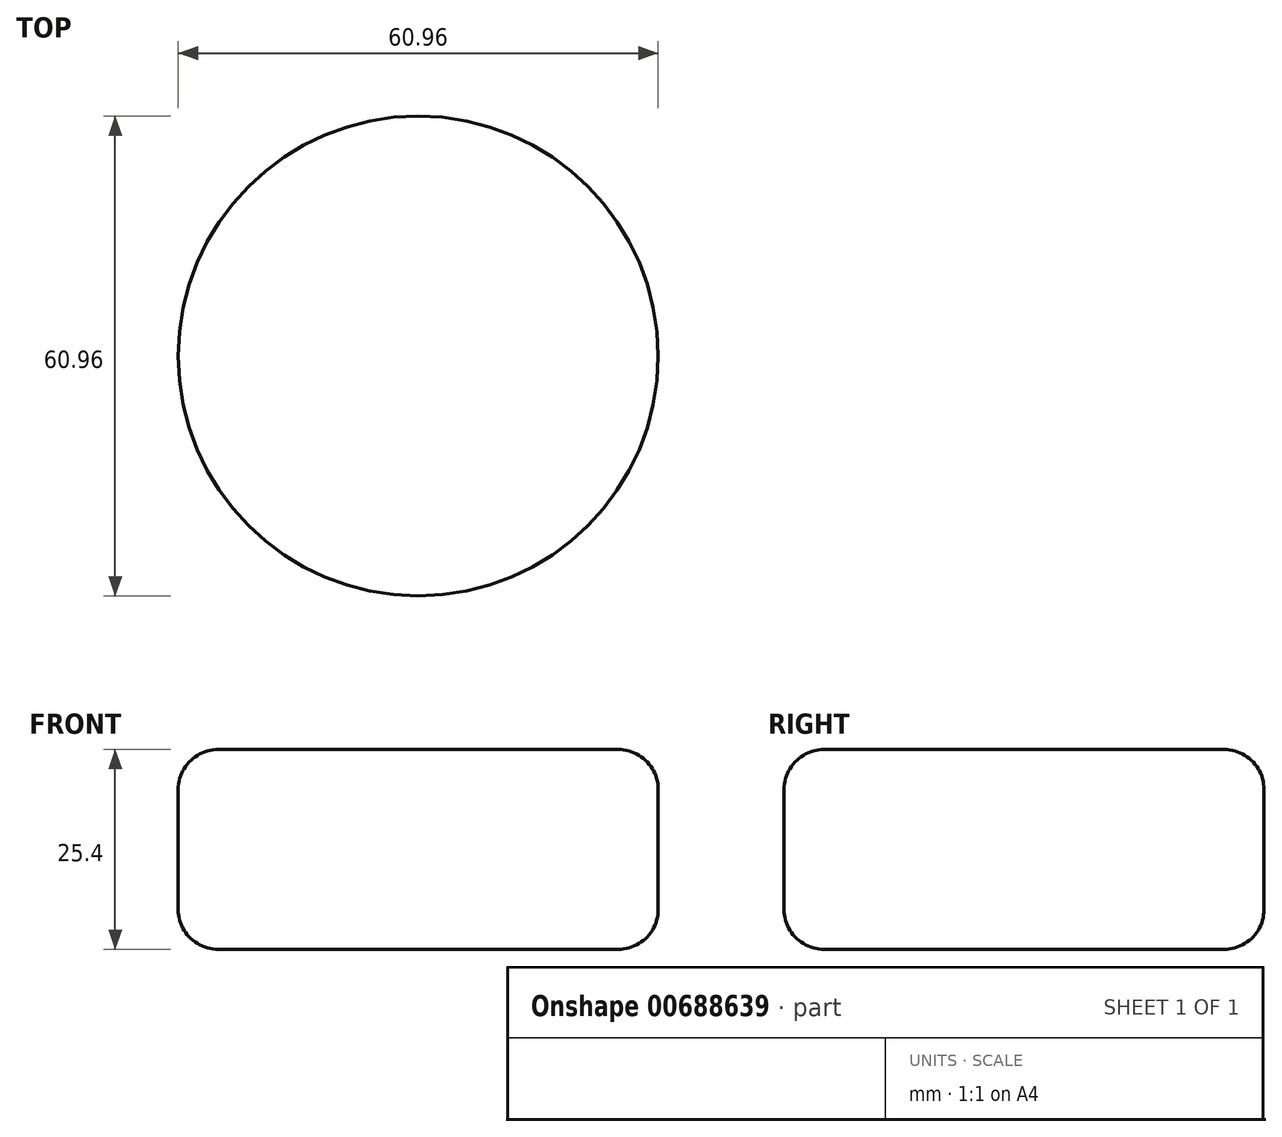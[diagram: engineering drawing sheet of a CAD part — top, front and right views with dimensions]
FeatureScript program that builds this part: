
annotation { "Feature Type Name" : "Feature", "Feature Type Description" : "" }
export const myFeature = defineFeature(function(context is Context, id is Id, definition is map)
    precondition{}
    {
        {
            var Q0;
            Q0=qCreatedBy(makeId("Top.planeOp"),FACE);
            var sketch = newSketch(context, id + "F0", { "sketchPlane" : qUnion([Q0])});
            skCircle(sketch, "E0", {"center": v(0, 0) * mm, "radius": 30.48 * mm});
            skSolve(sketch);
        }
        {
            var Q0;
            Q0 = qSketchRegion(id + "F0", true);
            extrude(context, id + "F1", {"entities" : qUnion([Q0]), "depth" : 25.4 * mm, "offsetDistance" : 25.4 * mm});
        }
        {
            var Q0;
            Q0=makeQuery(id+"F1.opExtrude","CAP_EDGE",EDGE,{"disambiguationData":[OSD([sQuery(id+"F0.wireOp",EDGE,"E0")])],"isStart":false});
            var Q1;
            Q1=makeQuery(id+"F1.opExtrude","SWEPT_FACE",FACE,{"disambiguationData":[OSD([sQuery(id+"F0.wireOp",EDGE,"E0")])]});
            fillet(context, id + "F2", {"entities" : qUnion([Q0, Q1]), "radius" : 5.08 * mm, "tangentPropagation" : true, "allowEdgeOverflow" : false});
        }
    });
